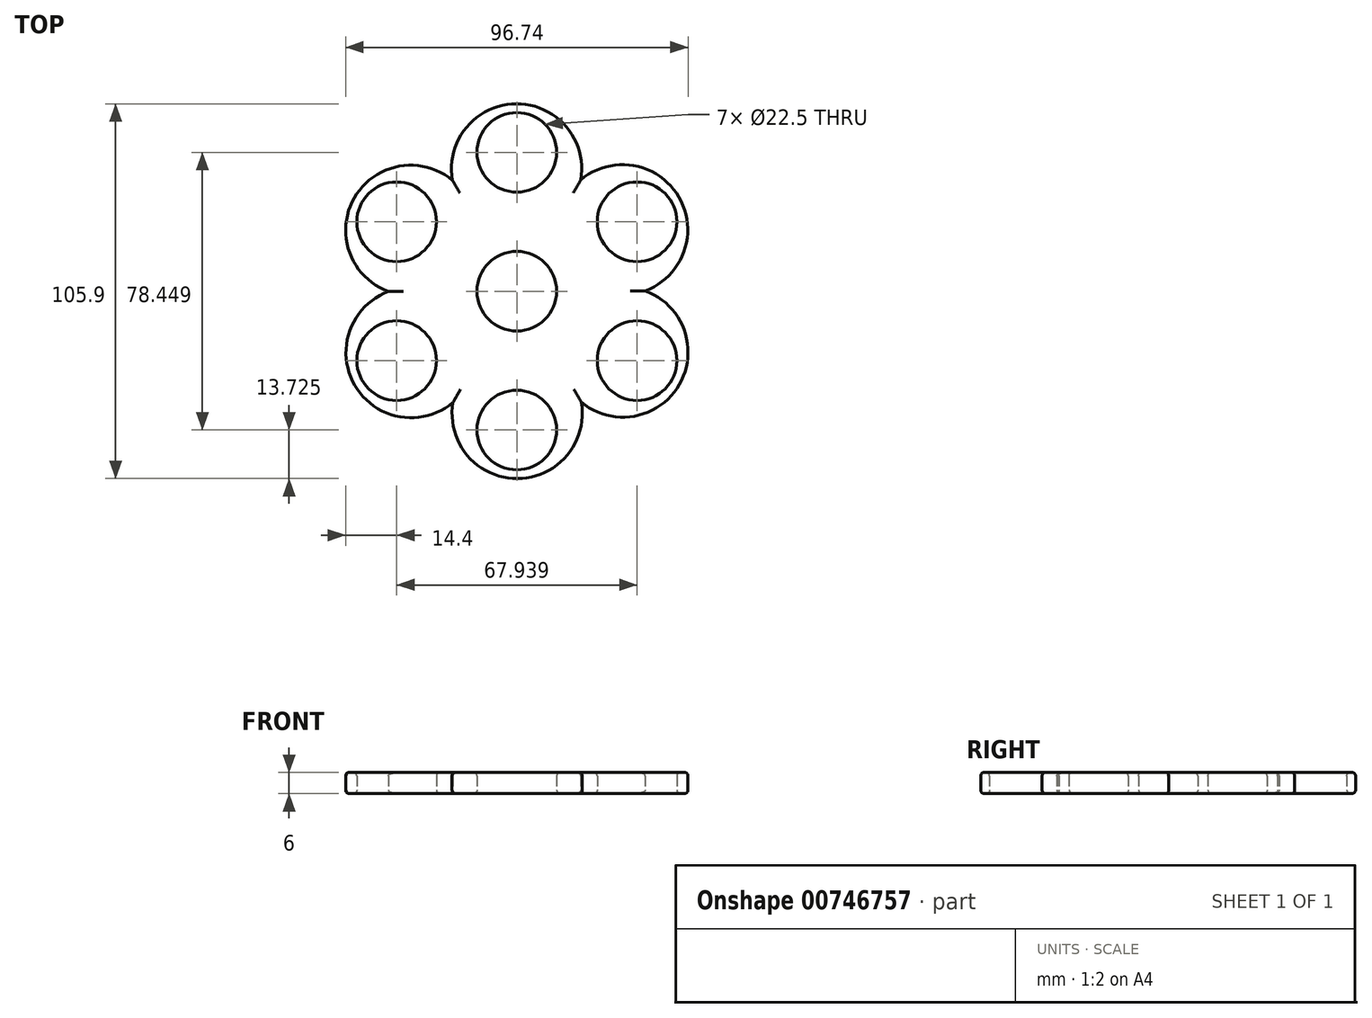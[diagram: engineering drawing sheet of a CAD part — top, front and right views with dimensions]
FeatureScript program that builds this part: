
annotation { "Feature Type Name" : "Feature", "Feature Type Description" : "" }
export const myFeature = defineFeature(function(context is Context, id is Id, definition is map)
    precondition{}
    {
        {
            var Q0;
            Q0=qCreatedBy(makeId("Top.planeOp"),FACE);
            var sketch = newSketch(context, id + "F0", { "sketchPlane" : qUnion([Q0])});
            skCircle(sketch, "E0", {"center": v(0, 0) * mm, "radius": 11.25 * mm});
            skCircle(sketch, "E1", {"center": v(0, 39.22) * mm, "radius": 11.25 * mm});
            skCircle(sketch, "E2.1.0", {"center": v(-33.97, 19.61) * mm, "radius": 11.25 * mm});
            skCircle(sketch, "E2.2.0", {"center": v(-33.97, -19.61) * mm, "radius": 11.25 * mm});
            skCircle(sketch, "E2.3.0", {"center": v(0, -39.22) * mm, "radius": 11.25 * mm});
            skCircle(sketch, "E2.4.0", {"center": v(33.97, -19.61) * mm, "radius": 11.25 * mm});
            skCircle(sketch, "E2.5.0", {"center": v(33.97, 19.61) * mm, "radius": 11.25 * mm});
            skArc(sketch, "E3", {"start": v(15.62, 24.95) * mm, "mid": v(1.29, 52.9) * mm, "end": v(-17.05, 27.4) * mm});
            skArc(sketch, "E4.1.0", {"start": v(-13.8, 26) * mm, "mid": v(-45.17, 27.57) * mm, "end": v(-32.26, -1.06) * mm});
            skArc(sketch, "E4.2.0", {"start": v(-29.42, 1.05) * mm, "mid": v(-46.46, -25.34) * mm, "end": v(-15.2, -28.47) * mm});
            skArc(sketch, "E4.3.0", {"start": v(-15.62, -24.95) * mm, "mid": v(-1.29, -52.9) * mm, "end": v(17.05, -27.4) * mm});
            skArc(sketch, "E4.4.0", {"start": v(13.8, -26) * mm, "mid": v(45.17, -27.57) * mm, "end": v(32.26, 1.06) * mm});
            skArc(sketch, "E4.5.0", {"start": v(29.42, -1.05) * mm, "mid": v(46.46, 25.34) * mm, "end": v(15.2, 28.47) * mm});
            skSolve(sketch);
        }
        {
            var Q0;
            Q0=makeQuery(id+"F0.imprint","IMPRINT",FACE,{"disambiguationData":[TD([[makeQuery(id+"F0.imprint","IMPRINT",EDGE,{"derivedFrom":sQuery(id+"F0.wireOp",EDGE,"E0")}),-1.0]])]});
            extrude(context, id + "F1", {"entities" : qUnion([Q0]), "depth" : 6 * mm, "offsetDistance" : 25 * mm});
        }
        {
            var Q0;
            Q0=makeQuery(id+"F1.opExtrude","CAP_EDGE",EDGE,{"disambiguationData":[OSD([sQuery(id+"F0.wireOp",EDGE,"E4.3.0")])],"isStart":false});
            var Q1;
            Q1=makeQuery(id+"F1.opExtrude","CAP_EDGE",EDGE,{"disambiguationData":[OSD([sQuery(id+"F0.wireOp",EDGE,"E4.4.0")])],"isStart":false});
            var Q2;
            Q2=makeQuery(id+"F1.opExtrude","CAP_EDGE",EDGE,{"disambiguationData":[OSD([sQuery(id+"F0.wireOp",EDGE,"E4.4.0")])],"isStart":true});
            var Q3;
            Q3=makeQuery(id+"F1.opExtrude","CAP_EDGE",EDGE,{"disambiguationData":[OSD([sQuery(id+"F0.wireOp",EDGE,"E4.3.0")])],"isStart":true});
            var Q4;
            Q4=makeQuery(id+"F1.opExtrude","CAP_EDGE",EDGE,{"disambiguationData":[OSD([sQuery(id+"F0.wireOp",EDGE,"E4.5.0")])],"isStart":false});
            var Q5;
            Q5=makeQuery(id+"F1.opExtrude","CAP_EDGE",EDGE,{"disambiguationData":[OSD([sQuery(id+"F0.wireOp",EDGE,"E4.5.0")])],"isStart":true});
            var Q6;
            Q6=makeQuery(id+"F1.opExtrude","CAP_FACE",FACE,{"disambiguationData":[OSD([sQuery(id+"F0.wireOp",EDGE,"E0"),sQuery(id+"F0.wireOp",EDGE,"E1"),sQuery(id+"F0.wireOp",EDGE,"E2.1.0"),sQuery(id+"F0.wireOp",EDGE,"E2.2.0"),sQuery(id+"F0.wireOp",EDGE,"E2.3.0"),sQuery(id+"F0.wireOp",EDGE,"E2.4.0"),sQuery(id+"F0.wireOp",EDGE,"E2.5.0"),sQuery(id+"F0.wireOp",EDGE,"E3"),sQuery(id+"F0.wireOp",EDGE,"E4.1.0"),sQuery(id+"F0.wireOp",EDGE,"E4.2.0"),sQuery(id+"F0.wireOp",EDGE,"E4.3.0"),sQuery(id+"F0.wireOp",EDGE,"E4.4.0"),sQuery(id+"F0.wireOp",EDGE,"E4.5.0")])],"isStart":false});
            var Q7;
            Q7=makeQuery(id+"F1.opExtrude","CAP_FACE",FACE,{"disambiguationData":[OSD([sQuery(id+"F0.wireOp",EDGE,"E0"),sQuery(id+"F0.wireOp",EDGE,"E1"),sQuery(id+"F0.wireOp",EDGE,"E2.1.0"),sQuery(id+"F0.wireOp",EDGE,"E2.2.0"),sQuery(id+"F0.wireOp",EDGE,"E2.3.0"),sQuery(id+"F0.wireOp",EDGE,"E2.4.0"),sQuery(id+"F0.wireOp",EDGE,"E2.5.0"),sQuery(id+"F0.wireOp",EDGE,"E3"),sQuery(id+"F0.wireOp",EDGE,"E4.1.0"),sQuery(id+"F0.wireOp",EDGE,"E4.2.0"),sQuery(id+"F0.wireOp",EDGE,"E4.3.0"),sQuery(id+"F0.wireOp",EDGE,"E4.4.0"),sQuery(id+"F0.wireOp",EDGE,"E4.5.0")])],"isStart":true});
            fillet(context, id + "F2", {"entities" : qUnion([Q0, Q1, Q2, Q3, Q4, Q5, Q6, Q7]), "radius" : 1 * mm, "tangentPropagation" : true, "allowEdgeOverflow" : false});
        }
    });
